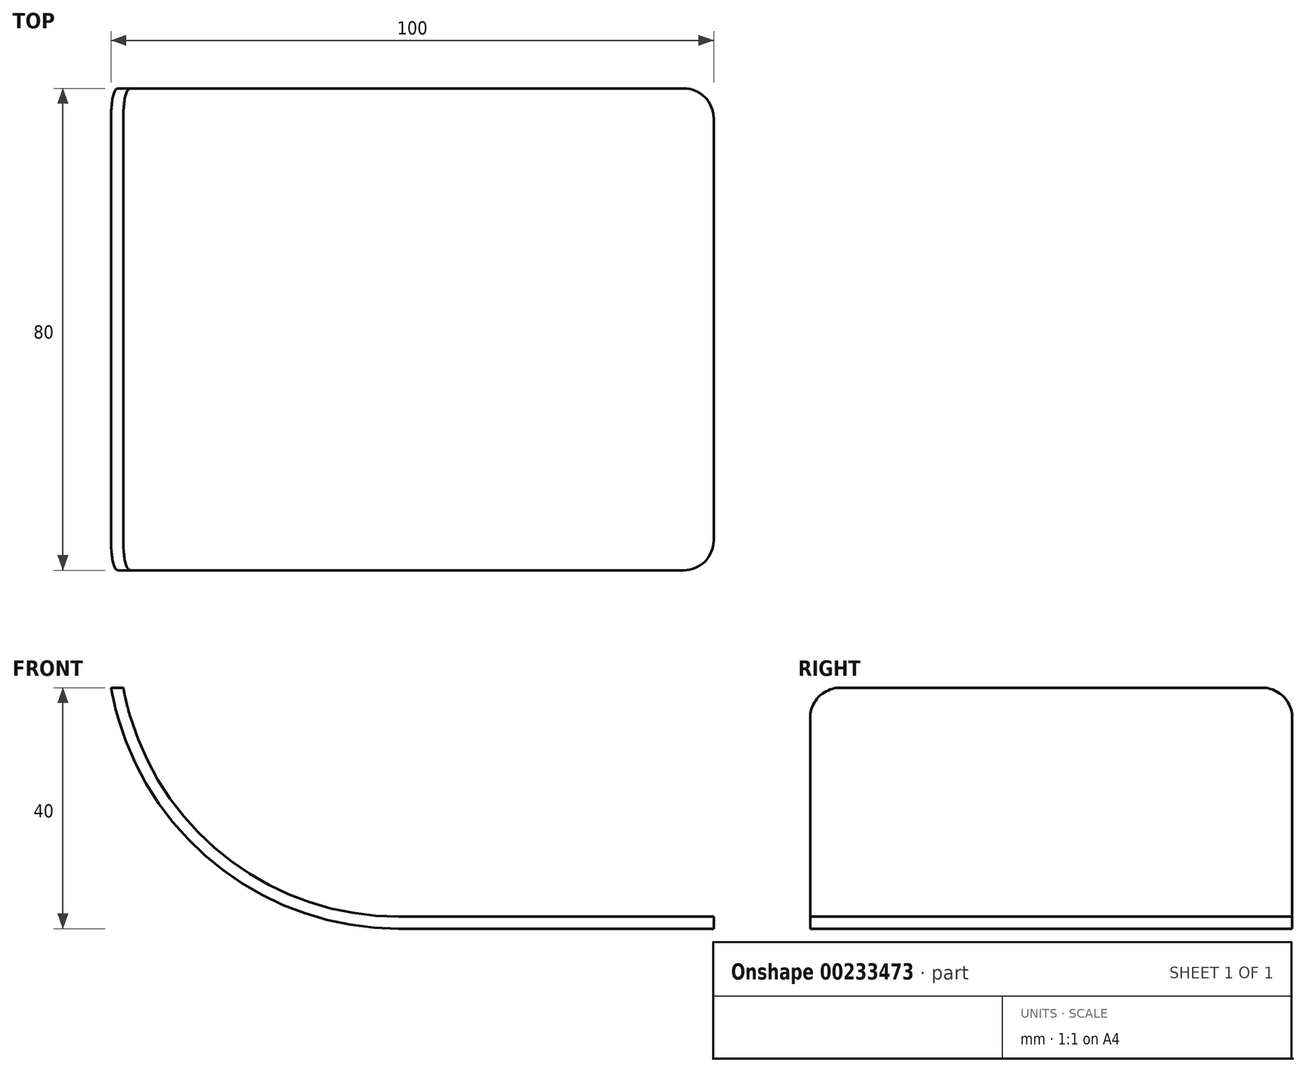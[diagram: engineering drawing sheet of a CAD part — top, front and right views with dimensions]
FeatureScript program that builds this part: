
annotation { "Feature Type Name" : "Feature", "Feature Type Description" : "" }
export const myFeature = defineFeature(function(context is Context, id is Id, definition is map)
    precondition{}
    {
        {
            var Q0;
            Q0=qCreatedBy(makeId("Front.planeOp"),FACE);
            var sketch = newSketch(context, id + "F0", { "sketchPlane" : qUnion([Q0])});
            skLineSegment(sketch, "E0", {"start": v(0, 0) * mm, "end": v(-52.33, 0) * mm});
            skLineSegment(sketch, "E1", {"start": v(-100, 40) * mm, "end": v(-103.8, 61.59) * mm, "construction": true});
            skArc(sketch, "E2", {"start": v(-52.33, 0) * mm, "mid": v(-83.44, 11.32) * mm, "end": v(-100, 40) * mm});
            skLineSegment(sketch, "E3", {"start": v(0, 0) * mm, "end": v(0, 20.65) * mm, "construction": true});
            skArc(sketch, "E4.0", {"start": v(-52.33, 2) * mm, "mid": v(-82.02, 12.74) * mm, "end": v(-97.97, 40) * mm});
            skLineSegment(sketch, "E4.1", {"start": v(0, 2) * mm, "end": v(-52.33, 2) * mm});
            skLineSegment(sketch, "E5", {"start": v(-100, 40) * mm, "end": v(-97.97, 40) * mm});
            skLineSegment(sketch, "E6", {"start": v(0, 2) * mm, "end": v(0, 0) * mm});
            skLineSegment(sketch, "E7", {"start": v(25.03, -0.7) * mm, "end": v(25.03, 27.63) * mm, "construction": true});
            skLineSegment(sketch, "E8.MirrorCS", {"start": v(50.06, 2) * mm, "end": v(102.4, 2) * mm, "construction": true});
            skArc(sketch, "E9.MirrorCS", {"start": v(102.4, 2) * mm, "mid": v(132.09, 12.74) * mm, "end": v(148.03, 40) * mm, "construction": true});
            skArc(sketch, "E10.MirrorCS", {"start": v(102.4, 0) * mm, "mid": v(133.5, 11.32) * mm, "end": v(150.06, 40) * mm, "construction": true});
            skLineSegment(sketch, "E11.MirrorCS", {"start": v(50.06, 0) * mm, "end": v(102.4, 0) * mm, "construction": true});
            skLineSegment(sketch, "E12.MirrorCS", {"start": v(150.06, 40) * mm, "end": v(148.03, 40) * mm, "construction": true});
            skLineSegment(sketch, "E13", {"start": v(50.06, 2) * mm, "end": v(50.06, 0) * mm, "construction": true});
            skLineSegment(sketch, "E14", {"start": v(-44.97, 38.96) * mm, "end": v(-44.97, -14.07) * mm, "construction": true});
            skLineSegment(sketch, "E15", {"start": v(95.03, 40.11) * mm, "end": v(95.03, -16.87) * mm, "construction": true});
            skSolve(sketch);
        }
        {
            var Q0;
            Q0 = qSketchRegion(id + "F0", true);
            extrude(context, id + "F1", {"entities" : qUnion([Q0]), "offsetDistance" : 25 * mm, "depth" : 80 * mm});
        }
        {
            var Q0;
            Q0=makeQuery(id+"F1.opExtrude","CAP_EDGE",EDGE,{"disambiguationData":[OSD([sQuery(id+"F0.wireOp",EDGE,"E5")])],"isStart":false});
            var Q1;
            Q1=makeQuery(id+"F1.opExtrude","CAP_EDGE",EDGE,{"disambiguationData":[OSD([sQuery(id+"F0.wireOp",EDGE,"E5")])],"isStart":true});
            var Q2;
            Q2=makeQuery(id+"F1.opExtrude","CAP_EDGE",EDGE,{"disambiguationData":[OSD([sQuery(id+"F0.wireOp",EDGE,"E6")])],"isStart":false});
            var Q3;
            Q3=makeQuery(id+"F1.opExtrude","CAP_EDGE",EDGE,{"disambiguationData":[OSD([sQuery(id+"F0.wireOp",EDGE,"E6")])],"isStart":true});
            fillet(context, id + "F2", {"entities" : qUnion([Q0, Q1, Q2, Q3]), "radius" : 5 * mm, "tangentPropagation" : true, "allowEdgeOverflow" : false});
        }
    });
